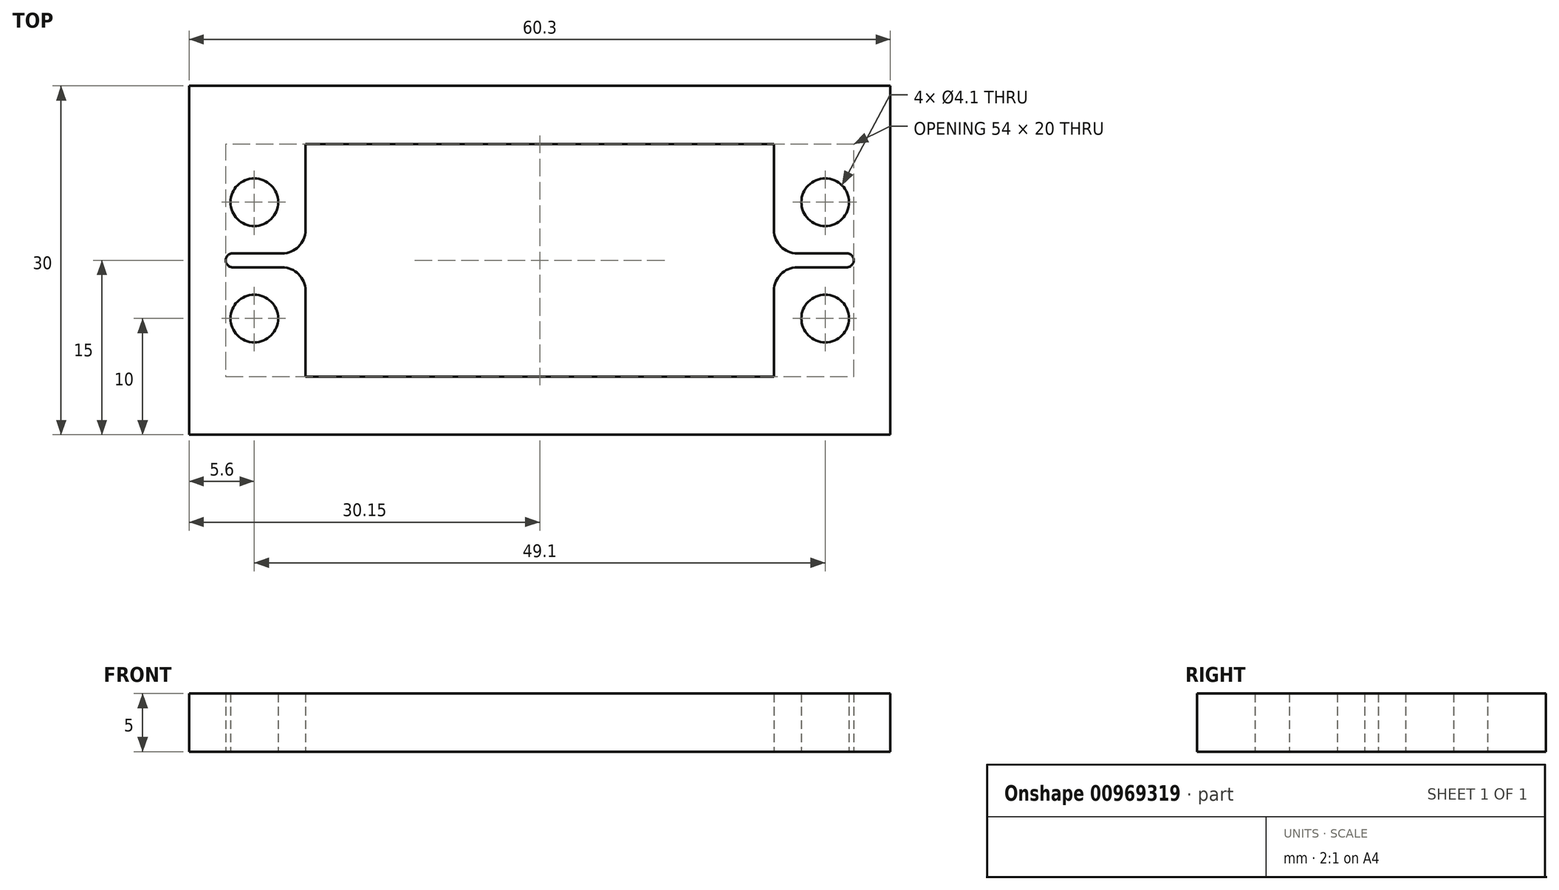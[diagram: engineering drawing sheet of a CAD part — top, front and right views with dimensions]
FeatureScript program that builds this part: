
annotation { "Feature Type Name" : "Feature", "Feature Type Description" : "" }
export const myFeature = defineFeature(function(context is Context, id is Id, definition is map)
    precondition{}
    {
        {
            var Q0;
            Q0=qCreatedBy(makeId("Top.planeOp"),FACE);
            var sketch = newSketch(context, id + "F0", { "sketchPlane" : qUnion([Q0])});
            skLineSegment(sketch, "E0.bottom", {"start": v(30.15, -15) * mm, "end": v(-30.15, -15) * mm});
            skLineSegment(sketch, "E0.top", {"start": v(30.15, 15) * mm, "end": v(-30.15, 15) * mm});
            skLineSegment(sketch, "E0.left", {"start": v(30.15, -15) * mm, "end": v(30.15, 15) * mm});
            skLineSegment(sketch, "E0.right", {"start": v(-30.15, -15) * mm, "end": v(-30.15, 15) * mm});
            skPoint(sketch, "E0.middle", {"position": v(0, 0) * mm});
            skLineSegment(sketch, "E1", {"start": v(0, 10) * mm, "end": v(20.15, 10) * mm});
            skLineSegment(sketch, "E2", {"start": v(20.15, 10) * mm, "end": v(20.15, 2.6) * mm});
            skLineSegment(sketch, "E3", {"start": v(22.15, 0.6) * mm, "end": v(26.4, 0.6) * mm});
            skLineSegment(sketch, "E4", {"start": v(27, 0) * mm, "end": v(27, 0) * mm});
            skPoint(sketch, "E5.visualSharp", {"position": v(27, 0.6) * mm});
            skArc(sketch, "E5.filletArc", {"start": v(27, 0) * mm, "mid": v(26.82, 0.42) * mm, "end": v(26.4, 0.6) * mm});
            skCircle(sketch, "E6", {"center": v(24.55, 5) * mm, "radius": 2.05 * mm});
            skPoint(sketch, "E7.visualSharp", {"position": v(20.15, 0.6) * mm});
            skArc(sketch, "E7.filletArc", {"start": v(20.15, 2.6) * mm, "mid": v(20.74, 1.19) * mm, "end": v(22.15, 0.6) * mm});
            skArc(sketch, "E8.MirrorCS", {"start": v(-27, 0) * mm, "mid": v(-26.82, 0.42) * mm, "end": v(-26.4, 0.6) * mm});
            skLineSegment(sketch, "E9.MirrorCS", {"start": v(0, 10) * mm, "end": v(-20.15, 10) * mm});
            skPoint(sketch, "E10.MirrorP", {"position": v(-20.15, 0.6) * mm});
            skPoint(sketch, "E11.MirrorP", {"position": v(-27, 0.6) * mm});
            skArc(sketch, "E12.MirrorCS", {"start": v(-20.15, 2.6) * mm, "mid": v(-20.74, 1.19) * mm, "end": v(-22.15, 0.6) * mm});
            skLineSegment(sketch, "E13.MirrorCS", {"start": v(-20.15, 10) * mm, "end": v(-20.15, 2.6) * mm});
            skLineSegment(sketch, "E14.MirrorCS", {"start": v(-22.15, 0.6) * mm, "end": v(-26.4, 0.6) * mm});
            skCircle(sketch, "E15.MirrorC", {"center": v(-24.55, 5) * mm, "radius": 2.05 * mm});
            skLineSegment(sketch, "E16.MirrorCS", {"start": v(-27, 0) * mm, "end": v(-27, 0) * mm});
            skArc(sketch, "E17.MirrorCS", {"start": v(27, 0) * mm, "mid": v(26.82, -0.42) * mm, "end": v(26.4, -0.6) * mm});
            skArc(sketch, "E18.MirrorCS", {"start": v(-27, 0) * mm, "mid": v(-26.82, -0.42) * mm, "end": v(-26.4, -0.6) * mm});
            skArc(sketch, "E19.MirrorCS", {"start": v(-20.15, -2.6) * mm, "mid": v(-20.74, -1.19) * mm, "end": v(-22.15, -0.6) * mm});
            skArc(sketch, "E20.MirrorCS", {"start": v(20.15, -2.6) * mm, "mid": v(20.74, -1.19) * mm, "end": v(22.15, -0.6) * mm});
            skLineSegment(sketch, "E21.MirrorCS", {"start": v(-20.15, -10) * mm, "end": v(-20.15, -2.6) * mm});
            skCircle(sketch, "E22.MirrorC", {"center": v(24.55, -5) * mm, "radius": 2.05 * mm});
            skLineSegment(sketch, "E23.MirrorCS", {"start": v(0, -10) * mm, "end": v(-20.15, -10) * mm});
            skLineSegment(sketch, "E24.MirrorCS", {"start": v(-22.15, -0.6) * mm, "end": v(-26.4, -0.6) * mm});
            skPoint(sketch, "E25.MirrorP", {"position": v(27, -0.6) * mm});
            skCircle(sketch, "E26.MirrorC", {"center": v(-24.55, -5) * mm, "radius": 2.05 * mm});
            skPoint(sketch, "E27.MirrorP", {"position": v(-27, -0.6) * mm});
            skLineSegment(sketch, "E28.MirrorCS", {"start": v(0, -10) * mm, "end": v(20.15, -10) * mm});
            skLineSegment(sketch, "E29.MirrorCS", {"start": v(22.15, -0.6) * mm, "end": v(26.4, -0.6) * mm});
            skLineSegment(sketch, "E30.MirrorCS", {"start": v(20.15, -10) * mm, "end": v(20.15, -2.6) * mm});
            skPoint(sketch, "E31.MirrorP", {"position": v(-20.15, -0.6) * mm});
            skPoint(sketch, "E32.MirrorP", {"position": v(20.15, -0.6) * mm});
            skSolve(sketch);
        }
        {
            var Q0;
            Q0 = qSketchRegion(id + "F0", true);
            extrude(context, id + "F1", {"entities" : qUnion([Q0]), "depth" : 5 * mm, "offsetDistance" : 25 * mm});
        }
    });
